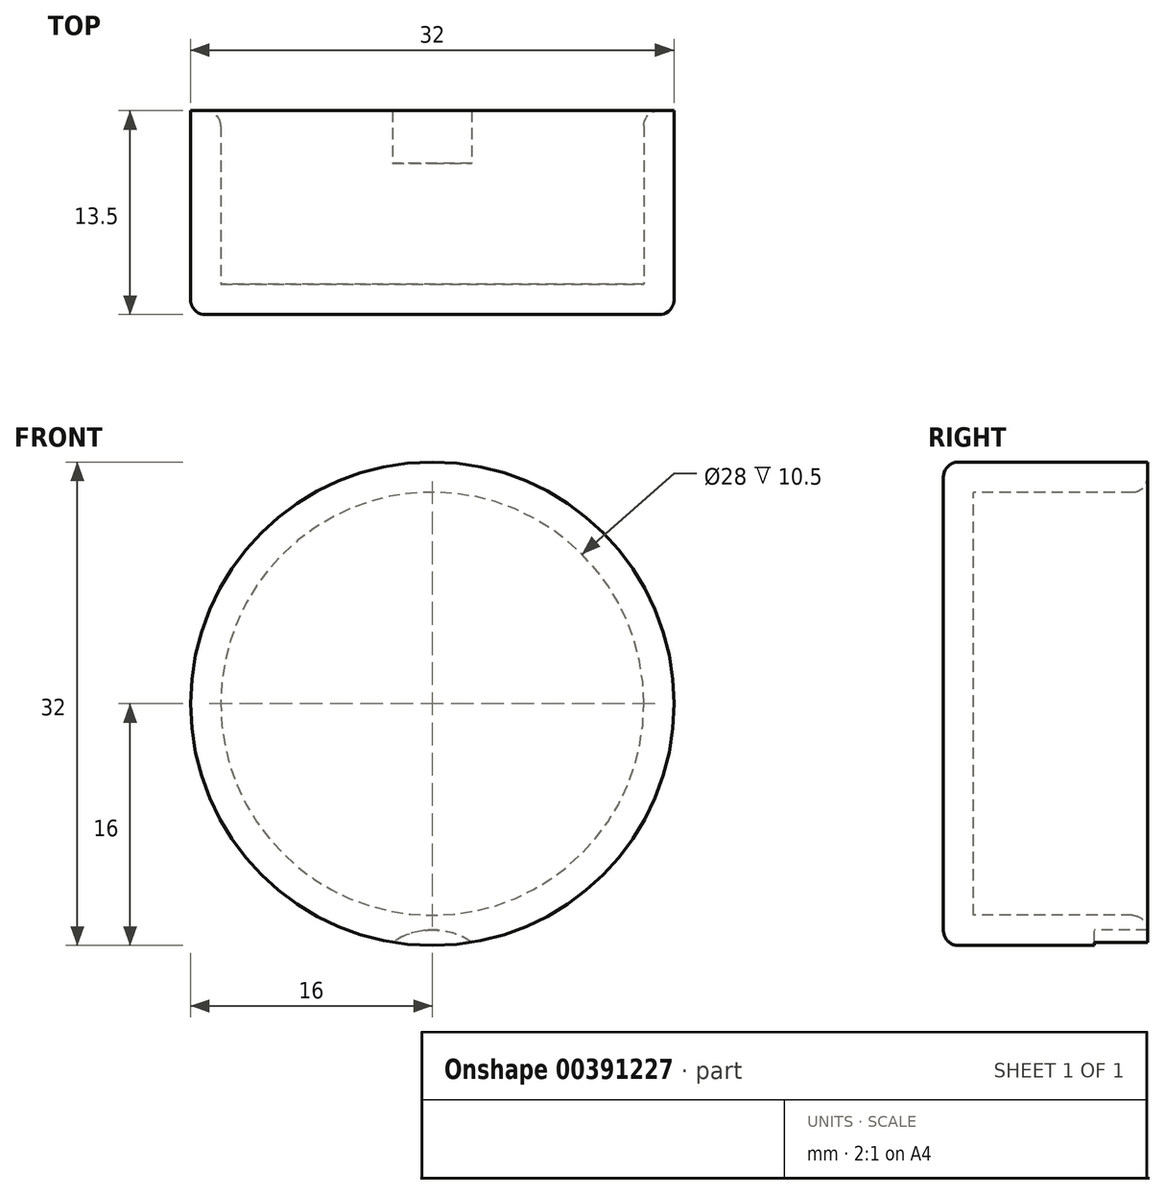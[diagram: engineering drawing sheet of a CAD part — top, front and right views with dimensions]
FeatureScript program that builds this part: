
annotation { "Feature Type Name" : "Feature", "Feature Type Description" : "" }
export const myFeature = defineFeature(function(context is Context, id is Id, definition is map)
    precondition{}
    {
        {
            var Q0;
            Q0=qCreatedBy(makeId("Front.planeOp"),FACE);
            var sketch = newSketch(context, id + "F0", { "sketchPlane" : qUnion([Q0])});
            skCircle(sketch, "E0", {"center": v(0, 0) * mm, "radius": 14 * mm});
            skCircle(sketch, "E1", {"center": v(0, 0) * mm, "radius": 16 * mm});
            skPoint(sketch, "E2", {"position": v(0, -14.98) * mm});
            skPoint(sketch, "E3", {"position": v(0, -24.28) * mm});
            skCircle(sketch, "E4", {"center": v(0, -19.63) * mm, "radius": 4.65 * mm});
            skPoint(sketch, "E4.third.point", {"position": v(3.42, -22.78) * mm});
            skSolve(sketch);
        }
        {
            var Q0;
            Q0=makeQuery(id+"F0.imprint","IMPRINT",FACE,{"disambiguationData":[TD([[makeQuery(id+"F0.imprint","IMPRINT",EDGE,{"derivedFrom":sQuery(id+"F0.wireOp",EDGE,"E0")}),-1.0]])]});
            extrude(context, id + "F1", {"entities" : qUnion([Q0]), "oppositeDirection" : true, "depth" : 3.5 * mm});
        }
        {
            var Q0;
            {var subQ0=sQuery(id+"F0.wireOp",EDGE,"E4");var subQ1=sQuery(id+"F0.wireOp",EDGE,"E1");var subQ2=makeQuery(id+"F0.imprint","INTERSECT",VERTEX,{"disambiguationData":[OD(0.0)],"derivedFrom":[subQ1,subQ0]});Q0=makeQuery(id+"F0.imprint","IMPRINT",FACE,{"disambiguationData":[TD([[makeQuery(id+"F0.imprint","IMPRINT",EDGE,{"disambiguationData":[TD([[subQ2,-1.0]])],"derivedFrom":subQ1}),1.0]])]});}
            var Q1;
            Q1=makeQuery(id+"F0.imprint","IMPRINT",FACE,{"disambiguationData":[TD([[makeQuery(id+"F0.imprint","IMPRINT",EDGE,{"derivedFrom":sQuery(id+"F0.wireOp",EDGE,"E0")}),-1.0]])]});
            extrude(context, id + "F2", {"entities" : qUnion([Q0, Q1]), "operationType" : NewBodyOperationType.ADD, "depth" : 10 * mm});
        }
        {
            var Q0;
            Q0=makeQuery(id+"F0.imprint","IMPRINT",FACE,{"disambiguationData":[TD([[makeQuery(id+"F0.imprint","IMPRINT",EDGE,{"derivedFrom":sQuery(id+"F0.wireOp",EDGE,"E0")}),1.0]])]});
            extrude(context, id + "F3", {"entities" : qUnion([Q0]), "operationType" : NewBodyOperationType.ADD, "depth" : 10 * mm, "hasSecondDirection" : true, "secondDirectionOppositeDirection" : false, "secondDirectionDepth" : 8 * mm});
        }
        {
            var Q0;
            Q0=makeQuery(id+"F2.opExtrude","CAP_EDGE",EDGE,{"disambiguationData":[OSD([sQuery(id+"F0.wireOp",EDGE,"E1")])],"isStart":false});
            var Q1;
            Q1=makeQuery(id+"F1.opExtrude","CAP_EDGE",EDGE,{"disambiguationData":[OSD([sQuery(id+"F0.wireOp",EDGE,"E0")])],"isStart":false});
            fillet(context, id + "F4", {"entities" : qUnion([Q0, Q1]), "radius" : 1 * mm, "tangentPropagation" : true, "allowEdgeOverflow" : false});
        }
    });
